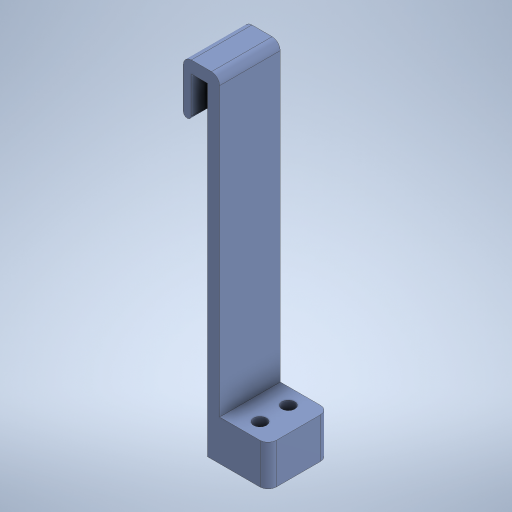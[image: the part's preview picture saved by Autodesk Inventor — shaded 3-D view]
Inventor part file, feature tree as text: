
AUTODESK INVENTOR PART (.ipt)
format: ipt  version: 2024.1 (Build 281209000, 209)  size: 288,768 bytes
history: native  units: mm
features: fillet x3, extrude x2, sketch x2
ambient origin geometry x8: Origin, YZ Plane, XZ Plane, XY Plane, X Axis, Y Axis, Z Axis, Center Point
bodies: Solide1 (feature_tree)
feature tree (7):
  extrude  "Extrusion1"  Depth=15.0mm TaperAngle=0.0deg
  extrude  "Extrusion2"  Depth=3.2mm
  fillet  "Congé2"  Radius=3.2mm
  fillet  "Congé3"  Radius=4.0mm
  fillet  "Congé4"  Radius=4.0mm
  sketch  "Esquisse1"
  sketch  "Esquisse2"
